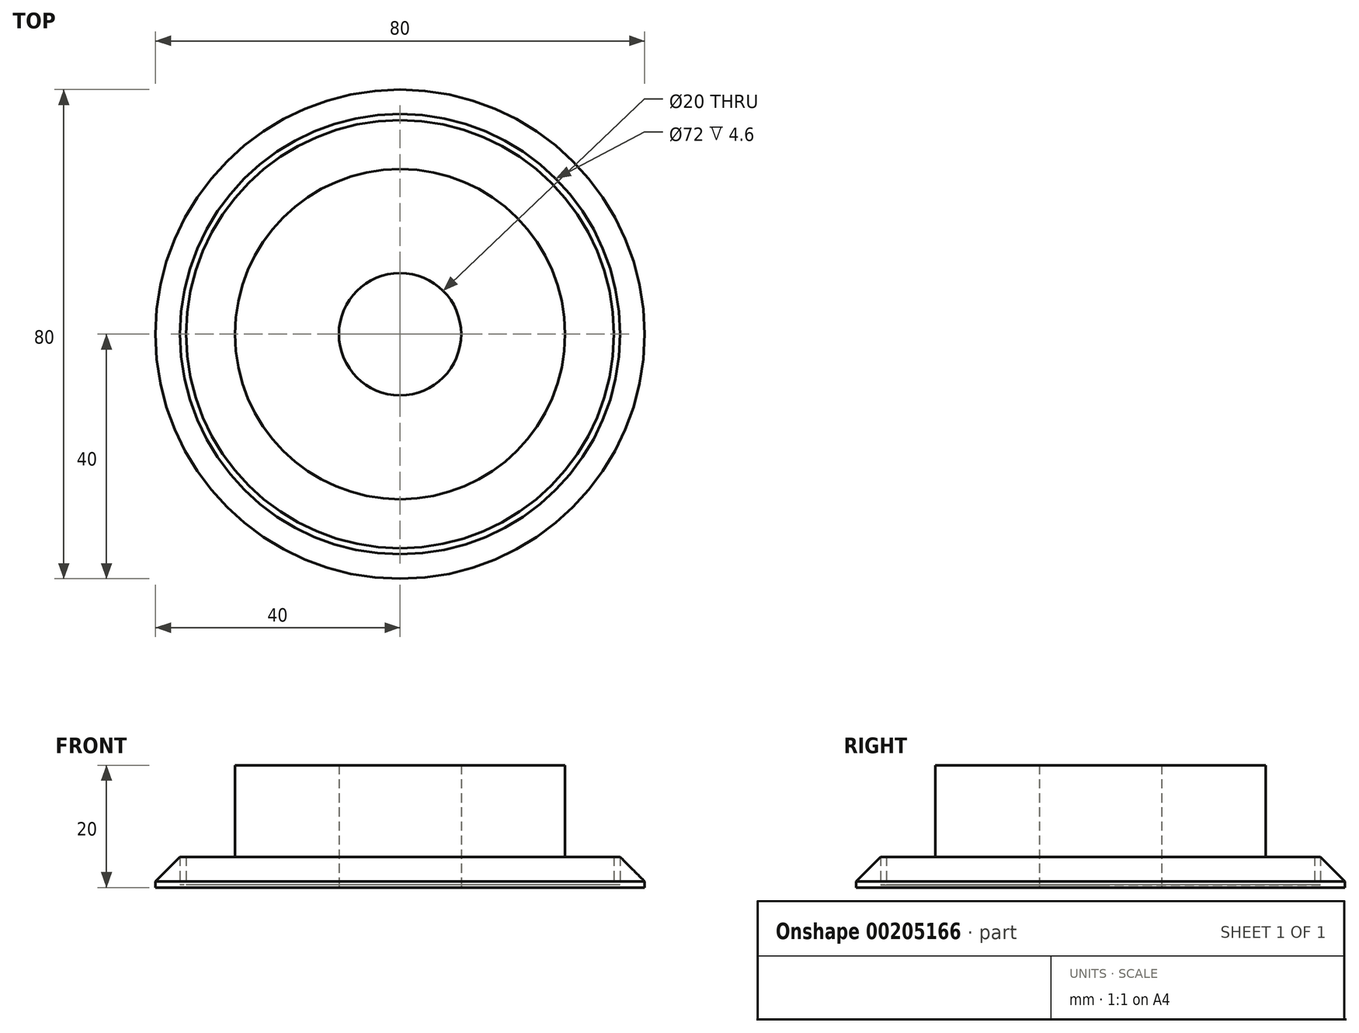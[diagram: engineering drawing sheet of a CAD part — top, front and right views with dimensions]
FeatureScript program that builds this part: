
annotation { "Feature Type Name" : "Feature", "Feature Type Description" : "" }
export const myFeature = defineFeature(function(context is Context, id is Id, definition is map)
    precondition{}
    {
        {
            var Q0;
            Q0=qCreatedBy(makeId("Top.planeOp"),FACE);
            var sketch = newSketch(context, id + "F0", { "sketchPlane" : qUnion([Q0])});
            skCircle(sketch, "E0", {"center": v(0, 0) * mm, "radius": 35 * mm});
            skCircle(sketch, "E1", {"center": v(0, 0) * mm, "radius": 10 * mm});
            skCircle(sketch, "E2", {"center": v(0, 0) * mm, "radius": 40 * mm});
            skSolve(sketch);
        }
        {
            var Q0;
            Q0=makeQuery(id+"F0.imprint","IMPRINT",FACE,{"disambiguationData":[TD([[makeQuery(id+"F0.imprint","IMPRINT",EDGE,{"derivedFrom":sQuery(id+"F0.wireOp",EDGE,"E0")}),1.0]])]});
            extrude(context, id + "F1", {"entities" : qUnion([Q0]), "depth" : 5 * mm});
        }
        {
            var Q0;
            Q0=makeQuery(id+"F1.opExtrude","CAP_FACE",FACE,{"disambiguationData":[OSD([sQuery(id+"F0.wireOp",EDGE,"E0"),sQuery(id+"F0.wireOp",EDGE,"E1")])],"isStart":false});
            var sketch = newSketch(context, id + "F2", { "sketchPlane" : qUnion([Q0])});
            skCircle(sketch, "E3", {"center": v(0, 0) * mm, "radius": 27 * mm});
            skSolve(sketch);
        }
        {
            var Q0;
            Q0=makeQuery(id+"F2.imprint","IMPRINT",FACE,{"disambiguationData":[TD([[makeQuery(id+"F2.imprint","IMPRINT",EDGE,{"derivedFrom":sQuery(id+"F2.wireOp",EDGE,"E3")}),1.0]])]});
            extrude(context, id + "F3", {"entities" : qUnion([Q0]), "operationType" : NewBodyOperationType.ADD, "depth" : 15 * mm});
        }
        {
            var Q0;
            Q0=makeQuery(id+"F0.imprint","IMPRINT",FACE,{"disambiguationData":[TD([[makeQuery(id+"F0.imprint","IMPRINT",EDGE,{"derivedFrom":sQuery(id+"F0.wireOp",EDGE,"E0")}),-1.0]])]});
            extrude(context, id + "F4", {"entities" : qUnion([Q0]), "operationType" : NewBodyOperationType.ADD, "depth" : 0.4 * mm});
        }
        {
            var Q0;
            Q0=makeQuery(id+"F4.opExtrude","CAP_FACE",FACE,{"disambiguationData":[OSD([sQuery(id+"F0.wireOp",EDGE,"E0"),sQuery(id+"F0.wireOp",EDGE,"E2")])],"isStart":false});
            var sketch = newSketch(context, id + "F5", { "sketchPlane" : qUnion([Q0])});
            skCircle(sketch, "E4", {"center": v(0, 0) * mm, "radius": 36 * mm});
            skSolve(sketch);
        }
        {
            var Q0;
            Q0=makeQuery(id+"F5.imprint","IMPRINT",FACE,{"disambiguationData":[TD([[makeQuery(id+"F5.imprint","IMPRINT",EDGE,{"derivedFrom":sQuery(id+"F5.wireOp",EDGE,"E4")}),-1.0]])]});
            extrude(context, id + "F6", {"entities" : qUnion([Q0]), "operationType" : NewBodyOperationType.ADD, "depth" : 4.6 * mm});
        }
        {
            var Q0;
            Q0=makeQuery(id+"F6.opExtrude","CAP_EDGE",EDGE,{"disambiguationData":[OSD([sQuery(id+"F0.wireOp",EDGE,"E2")])],"isStart":false});
            chamfer(context, id + "F7", {"entities" : qUnion([Q0]), "width" : 4 * mm, "tangentPropagation" : true});
        }
    });
